# Revit family: Electronics_Community-Point-Source_Biamp_Loudspeaker_IC6_1082WR
name_source: partatom
category: Communication Devices
units: mm (PartAtom-declared; Revit-internal decimal feet)

## family parameters
Cut with Voids When Loaded = No
Host = Face
Maintain Annotation Orientation = No
OmniClass Number = 23.85.10.11.14.14.14
OmniClass Title = Loudspeakers
Part Type = Normal
Room Calculation Point = No
Round Connector Dimension = Use Diameter
Shared = No

## types (12) — shared parameters
Default Elevation = 48 "
Depth = 10.63 "
Description = IC6-1082WR High Output 8-Inch Two-Way Installation Loudspeaker
Environmental = Outdoor:  IP55W per IEC 60529, MIL-STD-810G
Height = 18.75 "
Input Connection = Screw terminal block (5-position)
Manufacturer = Biamp
Mounting Points = M10 threaded inserts; M8 threaded inserts (rear)
Nominal Maximum SPL = Peak - 124 dB; Continious - 118 dB
Operating Environment = Indoor or Weather-Resistant Outdoor
Operating Mode = Low Impedance or 70V/100V models
Product Documentation Link = https://downloads.biamp.com
Product Page URL = https://www.biamp.com
Product data url = https://www.bimobject.com
Recommended Amplifers = 250W - 500W - 8 ohms,  (45V - 63V)
Transducers = LF 1 x 8 (203mm) ferrite driver, 1.8 (45mm) voice coil; HF 1 x 1 (25mm exit, 1.75 (44mm) voice coil, advanced polymer diaphragm, ferrite compression driver
URL = https://www.biamp.com
Width = 10.4 "

## per-type parameters (varying)
| type | Connector Description | Equalized Maximum SPL | Equalized Sensitivity | Gril Material | Housing Material | Model | Nominal Beamwidth  (H x V) | Nominal Sensitivity | Operating Range | Weight |
| IC6-1082WT96 G | Screw terminal block (5-position); 70/100V applications | Peak - 124 dB; Continious - 118 dB | 1W/1m - 94 dB; 2.83V - 94 dB | Biamp - Plastic - Gray(Grid) | Biamp - Plastic - Gray | IC6-1082WT96 G | 90° x  60° | 1W/1m - 95 dB; 2.83V - 95 dB | 53 Hz to 20 kHz | 23.20 lbf |
| IC6-1082WT96 W | Screw terminal block (5-position); 70/100V applications | Peak - 124 dB; Continious - 118 dB | 1W/1m - 94 dB; 2.83V - 94 dB | Biamp - Plastic - White(Grid) | Biamp - Plastic - White | IC6-1082WT96 W | 90° x  60° | 1W/1m - 95 dB; 2.83V - 95 dB | 53 Hz to 20 kHz | 23.20 lbf |
| IC6-1082WT96 B | Screw terminal block (5-position); 70/100V applications | Peak - 124 dB; Continious - 118 dB | 1W/1m - 94 dB; 2.83V - 94 dB | Biamp - Plastic - Black(Grid) | Biamp - Plastic - Black | IC6-1082WT96 B | 90° x  60° | 1W/1m - 95 dB; 2.83V - 95 dB | 53 Hz to 20 kHz | 23.20 lbf |
| IC6-1082WT26 G | Screw terminal block (5-position); 70/100V applications | Peak - 123 dB; Continious - 117 dB | 1W/1m - 93 dB; 2.83V - 93 dB | Biamp - Plastic - Gray(Grid) | Biamp - Plastic - Gray | IC6-1082WT26 G | 120° x  60° | 1W/1m - 94 dB; 2.83V - 94 dB | 52 Hz to 19.5 kHz | 23.20 lbf |
| IC6-1082WT26 W | Screw terminal block (5-position); 70/100V applications | Peak - 123 dB; Continious - 117 dB | 1W/1m - 93 dB; 2.83V - 93 dB | Biamp - Plastic - White(Grid) | Biamp - Plastic - White | IC6-1082WT26 W | 120° x  60° | 1W/1m - 94 dB; 2.83V - 94 dB | 52 Hz to 19.5 kHz | 23.20 lbf |
| IC6-1082WT26 B | Screw terminal block (5-position); 70/100V applications | Peak - 123 dB; Continious - 117 dB | 1W/1m - 93 dB; 2.83V - 93 dB | Biamp - Plastic - Black(Grid) | Biamp - Plastic - Black | IC6-1082WT26 B | 120° x  60° | 1W/1m - 94 dB; 2.83V - 94 dB | 52 Hz to 19.5 kHz | 23.20 lbf |
| IC6-1082WR26 G | Screw terminal block (5-position); Low impedance (8 ohm) | Peak - 123 dB; Continious - 117 dB | 1W/1m - 93 dB; 2.83V - 93 dB | Biamp - Plastic - Gray(Grid) | Biamp - Plastic - Gray | IC6-1082WR26 G | 120° x  60° | 1W/1m - 94 dB; 2.83V - 94 dB | 52 Hz to 19.5 kHz | 19.20 lbf |
| IC6-1082WR26 W | Screw terminal block (5-position); Low impedance (8 ohm) | Peak - 123 dB; Continious - 117 dB | 1W/1m - 93 dB; 2.83V - 93 dB | Biamp - Plastic - White(Grid) | Biamp - Plastic - White | IC6-1082WR26 W | 120° x  60° | 1W/1m - 94 dB; 2.83V - 94 dB | 52 Hz to 19.5 kHz | 19.20 lbf |
| IC6-1082WR26 B | Screw terminal block (5-position); Low impedance (8 ohm) | Peak - 123 dB; Continious - 117 dB | 1W/1m - 93 dB; 2.83V - 93 dB | Biamp - Plastic - Black(Grid) | Biamp - Plastic - Black | IC6-1082WR26 B | 120° x  60° | 1W/1m - 94 dB; 2.83V - 94 dB | 52 Hz to 19.5 kHz | 19.20 lbf |
| IC6-1082WR96 G | Screw terminal block (5-position); Low impedance (8 ohm) | Peak - 124 dB; Continious - 118 dB | 1W/1m - 94 dB; 2.83V - 94 dB | Biamp - Plastic - Gray(Grid) | Biamp - Plastic - Gray | IC6-1082WR96 | 90° x  60° | 1W/1m - 95 dB; 2.83V - 95 dB | 53 Hz to 20 kHz | 19.20 lbf |
| IC6-1082WR96 W | Screw terminal block (5-position); Low impedance (8 ohm) | Peak - 124 dB; Continious - 118 dB | 1W/1m - 94 dB; 2.83V - 94 dB | Biamp - Plastic - White(Grid) | Biamp - Plastic - White | IC6-1082WR96 | 90° x  60° | 1W/1m - 95 dB; 2.83V - 95 dB | 53 Hz to 20 kHz | 19.20 lbf |
| IC6-1082WR96 B | Screw terminal block (5-position); Low impedance (8 ohm) | Peak - 124 dB; Continious - 118 dB | 1W/1m - 94 dB; 2.83V - 94 dB | Biamp - Plastic - Black(Grid) | Biamp - Plastic - Black | IC6-1082WR96 | 90° x  60° | 1W/1m - 95 dB; 2.83V - 95 dB | 53 Hz to 20 kHz | 19.20 lbf |

## geometry (parser evidence)
native form markers: Sweep x2
no freeform markers — native parametric forms only
